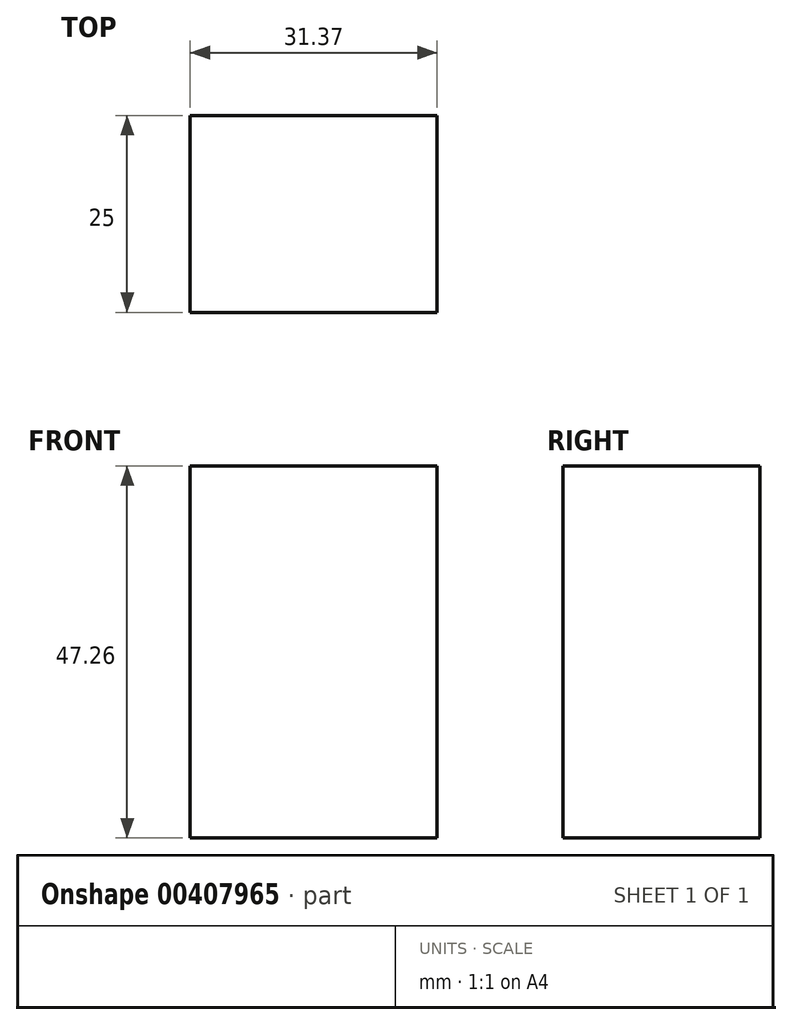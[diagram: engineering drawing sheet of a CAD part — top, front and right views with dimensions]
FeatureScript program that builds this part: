
annotation { "Feature Type Name" : "Feature", "Feature Type Description" : "" }
export const myFeature = defineFeature(function(context is Context, id is Id, definition is map)
    precondition{}
    {
        {
            var Q0;
            Q0=qCreatedBy(makeId("Front.planeOp"),FACE);
            var sketch = newSketch(context, id + "F0", { "sketchPlane" : qUnion([Q0])});
            skLineSegment(sketch, "E0.bottom", {"start": v(-84.69, 9.2) * mm, "end": v(-53.32, 9.2) * mm});
            skLineSegment(sketch, "E0.top", {"start": v(-84.69, 56.46) * mm, "end": v(-53.32, 56.46) * mm});
            skLineSegment(sketch, "E0.left", {"start": v(-84.69, 9.2) * mm, "end": v(-84.69, 56.46) * mm});
            skLineSegment(sketch, "E0.right", {"start": v(-53.32, 9.2) * mm, "end": v(-53.32, 56.46) * mm});
            skPoint(sketch, "E0.middle", {"position": v(-69, 32.83) * mm});
            skSolve(sketch);
        }
        {
            var Q0;
            Q0=makeQuery(id+"F0.imprint","IMPRINT",FACE,{"disambiguationData":[TD([[makeQuery(id+"F0.imprint","IMPRINT",EDGE,{"derivedFrom":sQuery(id+"F0.wireOp",EDGE,"E0.bottom")}),1.0]])]});
            extrude(context, id + "F1", {"entities" : qUnion([Q0]), "depth" : 25 * mm});
        }
    });
